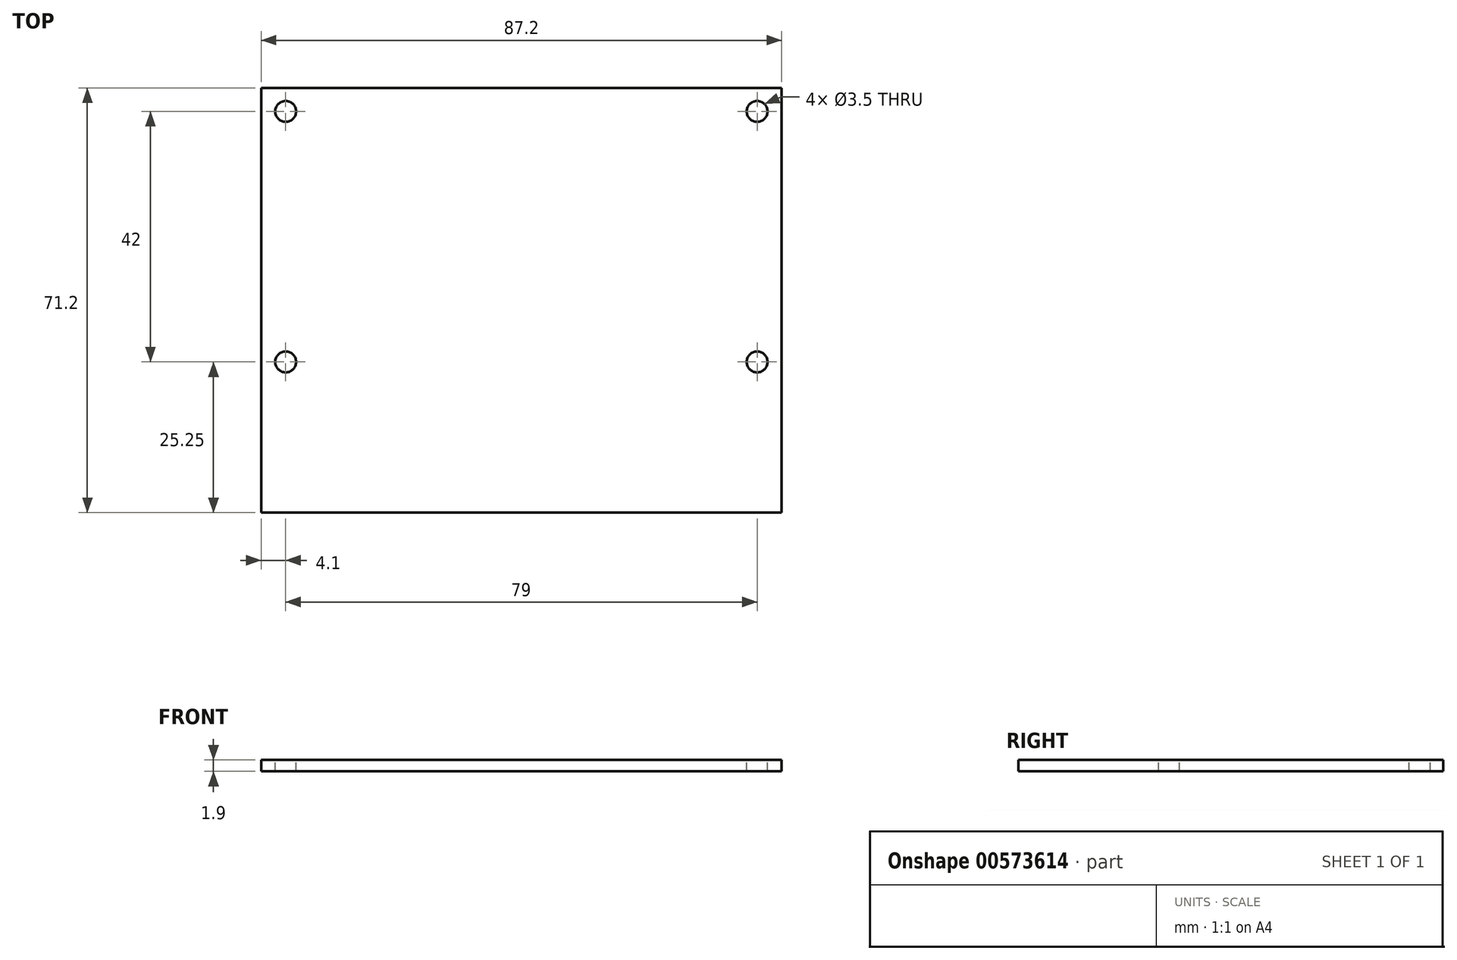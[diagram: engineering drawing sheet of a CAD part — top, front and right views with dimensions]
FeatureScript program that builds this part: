
annotation { "Feature Type Name" : "Feature", "Feature Type Description" : "" }
export const myFeature = defineFeature(function(context is Context, id is Id, definition is map)
    precondition{}
    {
        {
            var Q0;
            Q0=qCreatedBy(makeId("Top.planeOp"),FACE);
            var sketch = newSketch(context, id + "F0", { "sketchPlane" : qUnion([Q0])});
            skLineSegment(sketch, "E0.bottom", {"start": v(43.6, -35.6) * mm, "end": v(-43.6, -35.6) * mm});
            skLineSegment(sketch, "E0.top", {"start": v(43.6, 35.6) * mm, "end": v(-43.6, 35.6) * mm});
            skLineSegment(sketch, "E0.left", {"start": v(43.6, -35.6) * mm, "end": v(43.6, 35.6) * mm});
            skLineSegment(sketch, "E0.right", {"start": v(-43.6, -35.6) * mm, "end": v(-43.6, 35.6) * mm});
            skPoint(sketch, "E0.middle", {"position": v(0, 0) * mm});
            skSolve(sketch);
        }
        {
            var Q0;
            Q0 = qSketchRegion(id + "F0", true);
            extrude(context, id + "F1", {"entities" : qUnion([Q0]), "depth" : 1.9 * mm, "offsetDistance" : 25 * mm});
        }
        {
            var Q0;
            Q0=makeQuery(id+"F1.opExtrude","CAP_FACE",FACE,{"disambiguationData":[OSD([sQuery(id+"F0.wireOp",EDGE,"E0.bottom"),sQuery(id+"F0.wireOp",EDGE,"E0.top"),sQuery(id+"F0.wireOp",EDGE,"E0.left"),sQuery(id+"F0.wireOp",EDGE,"E0.right")])],"isStart":false});
            var sketch = newSketch(context, id + "F2", { "sketchPlane" : qUnion([Q0])});
            skLineSegment(sketch, "E1.bottom", {"start": v(-39.5, 31.65) * mm, "end": v(39.5, 31.65) * mm, "construction": true});
            skLineSegment(sketch, "E1.top", {"start": v(-39.5, -10.35) * mm, "end": v(39.5, -10.35) * mm, "construction": true});
            skLineSegment(sketch, "E1.left", {"start": v(-39.5, 31.65) * mm, "end": v(-39.5, -10.35) * mm, "construction": true});
            skLineSegment(sketch, "E1.right", {"start": v(39.5, 31.65) * mm, "end": v(39.5, -10.35) * mm, "construction": true});
            skCircle(sketch, "E2", {"center": v(-39.5, 31.65) * mm, "radius": 1.75 * mm});
            skCircle(sketch, "E3", {"center": v(39.5, 31.65) * mm, "radius": 1.75 * mm});
            skCircle(sketch, "E4", {"center": v(39.5, -10.35) * mm, "radius": 1.75 * mm});
            skCircle(sketch, "E5", {"center": v(-39.5, -10.35) * mm, "radius": 1.75 * mm});
            skLineSegment(sketch, "E6", {"start": v(0, 31.65) * mm, "end": v(0, -10.35) * mm, "construction": true});
            skSolve(sketch);
        }
        {
            var Q0;
            Q0 = qSketchRegion(id + "F2", true);
            extrude(context, id + "F3", {"entities" : qUnion([Q0]), "operationType" : NewBodyOperationType.REMOVE, "endBound" : BoundingType.UP_TO_NEXT, "oppositeDirection" : true, "depth" : 25 * mm, "offsetDistance" : 25 * mm});
        }
    });
